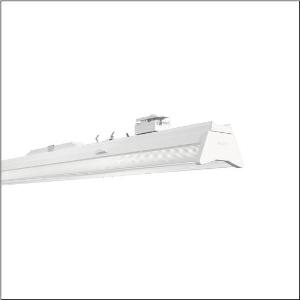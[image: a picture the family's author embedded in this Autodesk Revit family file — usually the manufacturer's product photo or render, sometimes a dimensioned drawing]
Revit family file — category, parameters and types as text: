
# Revit family: licross_r__21_performance_mo_52tm16cn36xg_705a
name_source: partatom
category: Lighting Fixtures
units: mm (PartAtom-declared; Revit-internal decimal feet)

## family parameters
Cut with Voids When Loaded = No
Host = Face
Light Source = No
Part Type = Normal
Room Calculation Point = No
Round Connector Dimension = Use Diameter
Shared = No

## types (1)
- --- (1 x LED, 6000 lm, 34.1 W, 3000K)
    Apparent Load = 34 VA
    CIE Flux Codes = 66 88 96 79 100
    Color Rendering = 80
    Color Temperature = 3000K
    Default Elevation = 1800 mm
    Description = Licross® 21 Performance MO, luminaire insert, of sheet steel, galvanised, coil coated, white, length: 1.500mm, width: 120mm, height: 123mm, LED rated luminous flux: 6.000lm, light colour: 830, SDCM (Standard Deviation of Colour Matching)MacAdam ≤ 3 SDCM (initial), control gear: ON/OFF Multilumen, CLOi, with plug, 3-pole, with phase selection, mains connection: 220..240V, AC, 50/60Hz, start of lifetime: 34W, end of service life: 40W, internal wiring halogen-free, primary light control with lens, of plastic, primary optical cover: cover, of PMMA, light emission: direct/indirect distribution, primary light characteristic: symmetric, protection rating (complete): IP40, insulation class (complete): insulation class I (protective earthing), certification: CE, ENEC, UKCA, protection symbol: D if used in an environment without relevant dust loads with corresponding accessories, impact resistance: IK06, permissible ambient temperature for indoor applications: -25..+55°C, corresponds to IFS (International Featured Standards) requirements for safety and quality in the food industry, reducing of maximum allowable ambient temperature of 5°C with ceiling mounting, LABS conformity tested according to VDMA 24364:2018-05, packaging unit: 1 piece
    Height = 114 mm
    Lamp = 1 x LED
    Lamp Light Flux = 6000 lm
    Lamp Power = 34.1 W
    Lamp count = 1
    Length = 1500 mm
    Luminous efficacy = 176 lm/W
    Manufacturer = Siteco
    ModVariant = No
    Model = 52TM16CN36XG
    Mounting Place = Ceiling
    Mounting Type = Pendant
    Number of Poles = 1
    OnlyDefault = Yes
    Power Factor = 1
    Product Name = Licross® 21 Performance MO
    Product group = luminaire insert | ceiling pendant
    ProductGroupID = 901
    Protection Class = Protection class I
    Protection Degree = IP 40
    RLX_Detail_Level = 1
    RLX_Emergency_Light_Flux = 0 lm
    RLX_Emergency_Type = 0
    RLX_Emergency_Type_DB = No
    RlxData = <blob elided: 31885 chars, md5=8bce6355>
    Socket = socket
    Standby Power = 0 W
    System Light Flux = 6000 lm
    System Power = 34 W
    Type Comments = factory setting: luminous flux: 100 % | (A | C | E) | 79 mA
    Type Image = l_1256138.jpg
    URL = http://relux.com
    VarID = @adj_019501
    Voltage = 0 V
    Weight = 0.00 kg
    Width = 120 mm

## geometry (parser evidence)
native form markers: Blend x4, Sweep x13
no freeform markers — native parametric forms only
